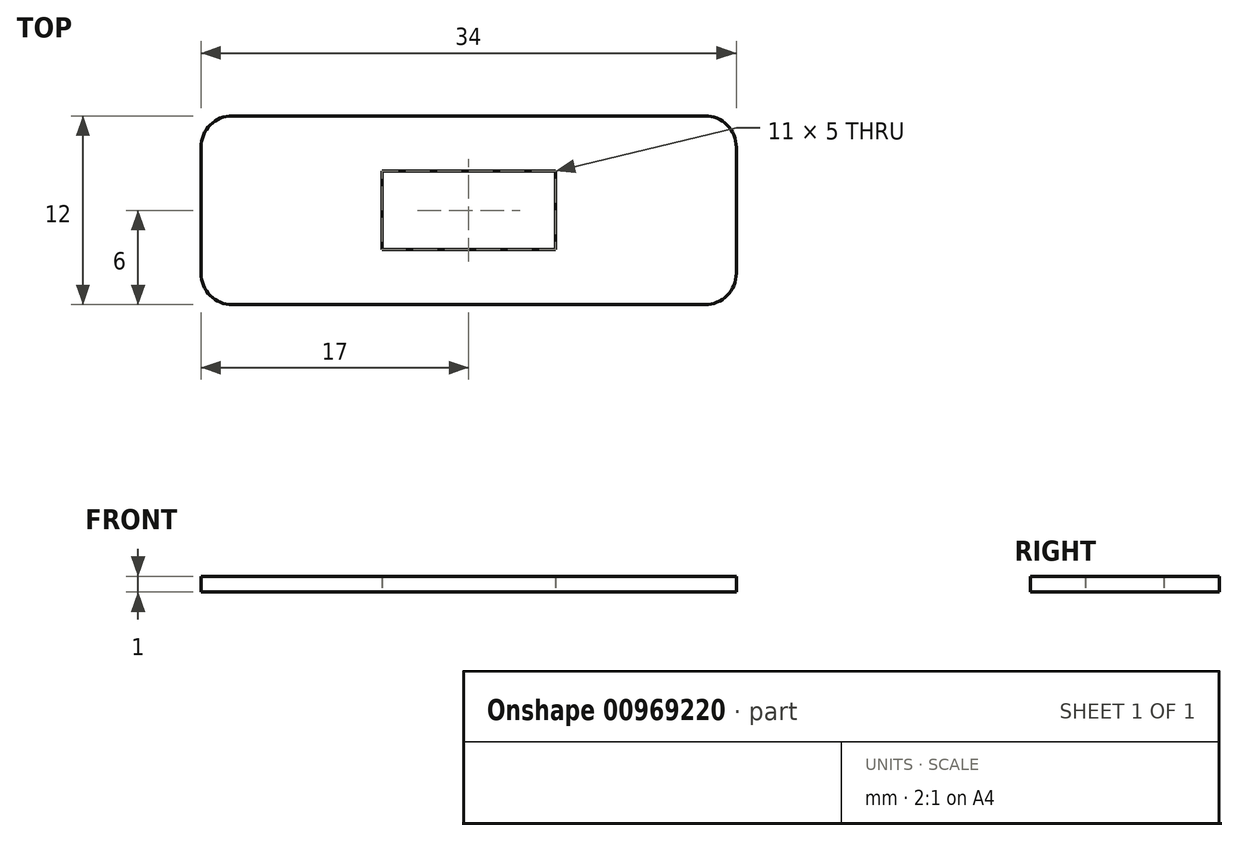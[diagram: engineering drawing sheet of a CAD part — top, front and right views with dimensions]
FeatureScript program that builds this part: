
annotation { "Feature Type Name" : "Feature", "Feature Type Description" : "" }
export const myFeature = defineFeature(function(context is Context, id is Id, definition is map)
    precondition{}
    {
        {
            var Q0;
            Q0=qCreatedBy(makeId("Top.planeOp"),FACE);
            var sketch = newSketch(context, id + "F0", { "sketchPlane" : qUnion([Q0])});
            skLineSegment(sketch, "E0.bottom", {"start": v(-2, 0) * mm, "end": v(-32, 0) * mm});
            skLineSegment(sketch, "E0.top", {"start": v(-2, 12) * mm, "end": v(-32, 12) * mm});
            skLineSegment(sketch, "E0.left", {"start": v(0, 2) * mm, "end": v(0, 10) * mm});
            skLineSegment(sketch, "E0.right", {"start": v(-34, 2) * mm, "end": v(-34, 10) * mm});
            skPoint(sketch, "E1.visualSharp", {"position": v(-34, 12) * mm});
            skArc(sketch, "E1.filletArc", {"start": v(-32, 12) * mm, "mid": v(-33.41, 11.41) * mm, "end": v(-34, 10) * mm});
            skPoint(sketch, "E2.visualSharp", {"position": v(-34, 0) * mm});
            skArc(sketch, "E2.filletArc", {"start": v(-34, 2) * mm, "mid": v(-33.41, 0.59) * mm, "end": v(-32, 0) * mm});
            skPoint(sketch, "E3.visualSharp", {"position": v(0, 12) * mm});
            skArc(sketch, "E3.filletArc", {"start": v(0, 10) * mm, "mid": v(-0.59, 11.41) * mm, "end": v(-2, 12) * mm});
            skPoint(sketch, "E4.visualSharp", {"position": v(0, 0) * mm});
            skArc(sketch, "E4.filletArc", {"start": v(-2, 0) * mm, "mid": v(-0.59, 0.59) * mm, "end": v(0, 2) * mm});
            skLineSegment(sketch, "E5.bottom", {"start": v(-22.5, 8.5) * mm, "end": v(-11.5, 8.5) * mm});
            skLineSegment(sketch, "E5.top", {"start": v(-22.5, 3.5) * mm, "end": v(-11.5, 3.5) * mm});
            skLineSegment(sketch, "E5.left", {"start": v(-22.5, 8.5) * mm, "end": v(-22.5, 3.5) * mm});
            skLineSegment(sketch, "E5.right", {"start": v(-11.5, 8.5) * mm, "end": v(-11.5, 3.5) * mm});
            skLineSegment(sketch, "E6", {"start": v(-17, 7.49) * mm, "end": v(-17, -1.85) * mm, "construction": true});
            skPoint(sketch, "E6.startSnap0", {"position": v(-17, 12) * mm});
            skSolve(sketch);
        }
        {
            var Q0;
            Q0=makeQuery(id+"F0.imprint","IMPRINT",FACE,{"disambiguationData":[TD([[makeQuery(id+"F0.imprint","IMPRINT",EDGE,{"derivedFrom":sQuery(id+"F0.wireOp",EDGE,"E0.bottom")}),-1.0]])]});
            extrude(context, id + "F1", {"entities" : qUnion([Q0]), "depth" : 1 * mm, "offsetDistance" : 25 * mm});
        }
    });
